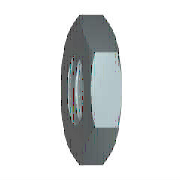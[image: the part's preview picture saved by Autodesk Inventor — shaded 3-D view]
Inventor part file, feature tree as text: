
AUTODESK INVENTOR PART (.ipt)
format: ipt  version: 2021 (Build 250183000, 183)  size: 168,960 bytes
history: native  units: mm (DEFAULTED — no unit token found)
features: sketch x3, chamfer x1, hole x1, other x1, plane x1
ambient origin geometry x7: Origin, YZ Plane, XZ Plane, X Axis, Y Axis, Z Axis, Center Point
bodies: Solid1 (feature_tree), Body (feature_tree)
feature tree (7):
  chamfer  "Chamfer1"  Angle=30.0deg  [1 undecoded]
  hole  "Thread"  [1 undecoded]
  other  "Work Axis1"
  plane  "Work Plane1"
  sketch  "Sketch1"  dims[d0=27.712813mm]
  sketch  "Sketch2"  dims[d1=8.0mm]
  sketch  "Sketch3"  dims[d2=0.0mm d3=30.0deg d4=30.0deg d5=22.5mm d6=22.5mm d7=90.0deg d25=13.835mm d26=6.0mm d27=4.0mm d28=2.0mm d29=14.3117mm d30=8.0mm d31=20.594885mm d8=1.082532mm d9=30.0deg d10=1.082532mm d11=30.0deg d13=0.0mm d14=0.0mm d39=0.0mm d40=1.082532mm d41=1.082532mm d42=0.0mm]
note: 2 required parameter values undecoded (feature->parameter linkage not recoverable at this tier; creation-order binding heuristic only, values carry confidence <= 0.55)
